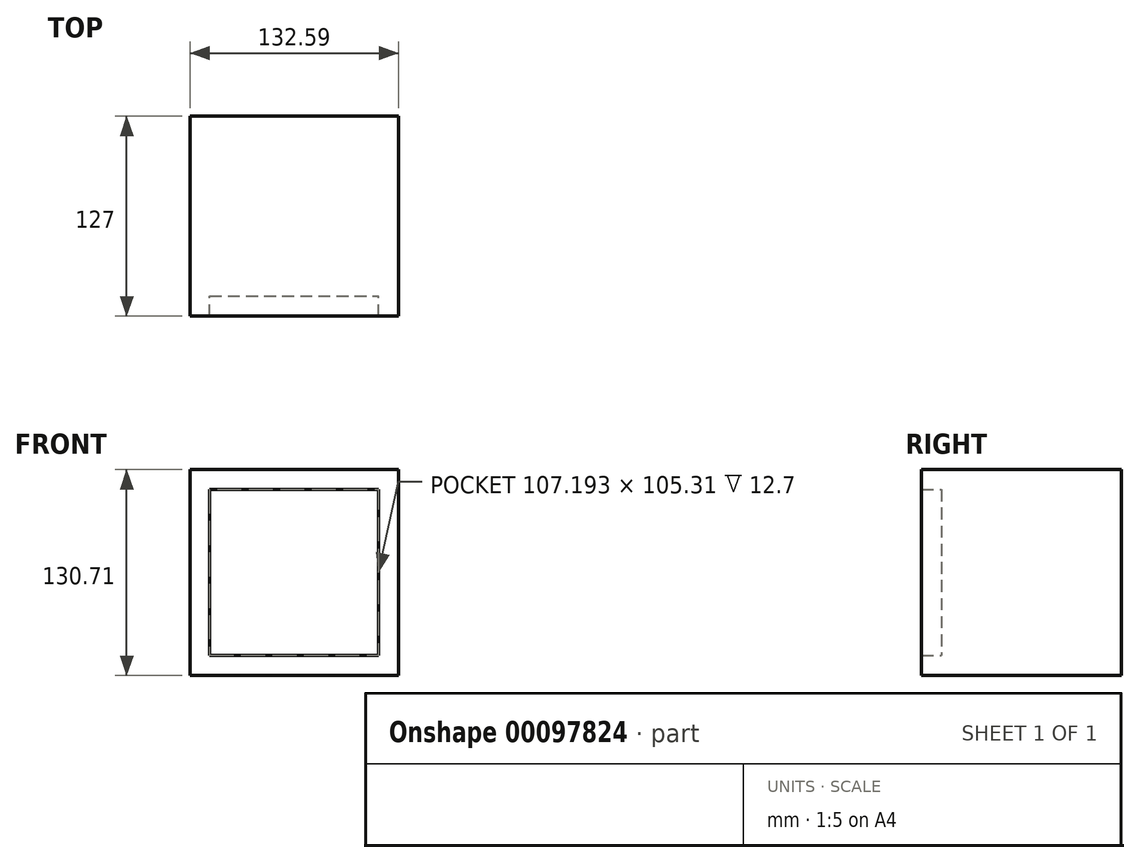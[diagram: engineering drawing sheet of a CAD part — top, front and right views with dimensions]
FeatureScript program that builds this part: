
annotation { "Feature Type Name" : "Feature", "Feature Type Description" : "" }
export const myFeature = defineFeature(function(context is Context, id is Id, definition is map)
    precondition{}
    {
        {
            var Q0;
            Q0=qCreatedBy(makeId("Front.planeOp"),FACE);
            var sketch = newSketch(context, id + "F3", { "sketchPlane" : qUnion([Q0])});
            skLineSegment(sketch, "E0.bottom", {"start": v(-65.8, 62.8) * mm, "end": v(66.78, 62.8) * mm});
            skLineSegment(sketch, "E0.top", {"start": v(-65.8, -67.92) * mm, "end": v(66.78, -67.92) * mm});
            skLineSegment(sketch, "E0.left", {"start": v(-65.8, 62.8) * mm, "end": v(-65.8, -67.92) * mm});
            skLineSegment(sketch, "E0.right", {"start": v(66.78, 62.8) * mm, "end": v(66.78, -67.92) * mm});
            skSolve(sketch);
        }
        {
            var Q0;
            Q0=makeQuery(id+"F3.imprint","IMPRINT",FACE,{"disambiguationData":[TD([[makeQuery(id+"F3.imprint","IMPRINT",EDGE,{"derivedFrom":sQuery(id+"F3.wireOp",EDGE,"E0.bottom")}),-1.0]])]});
            extrude(context, id + "F4", {"entities" : qUnion([Q0]), "depth" : 127 * mm});
        }
        {
            var Q0;
            Q0=makeQuery(id+"F4.opExtrude","CAP_FACE",FACE,{"disambiguationData":[OSD([sQuery(id+"F3.wireOp",EDGE,"E0.bottom"),sQuery(id+"F3.wireOp",EDGE,"E0.top"),sQuery(id+"F3.wireOp",EDGE,"E0.left"),sQuery(id+"F3.wireOp",EDGE,"E0.right")])],"isStart":false});
            shell(context, id + "F0", {"entities" : qUnion([Q0]), "thickness" : 12.7 * mm});
        }
        {
            var Q0;
            Q0=makeQuery(id+"F0.opShell","OFFSET_FACE",FACE,{"disambiguationData":[OSD([sQuery(id+"F3.wireOp",EDGE,"E0.bottom"),sQuery(id+"F3.wireOp",EDGE,"E0.top"),sQuery(id+"F3.wireOp",EDGE,"E0.left"),sQuery(id+"F3.wireOp",EDGE,"E0.right")])]});
            extrude(context, id + "F5", {"entities" : qUnion([Q0]), "operationType" : NewBodyOperationType.ADD, "depth" : 101.6 * mm});
        }
        {
            var Q0;
            Q0=qCreatedBy(makeId("Front.planeOp"),FACE);
            var sketch = newSketch(context, id + "F1", { "sketchPlane" : qUnion([Q0])});
            skCircle(sketch, "E1", {"center": v(0, -86.39) * mm, "radius": 5.77 * mm});
            skSolve(sketch);
        }
        {
            var Q0;
            Q0=sQuery(id+"F1.wireOp",EDGE,"E1");
            extrude(context, id + "F2", {"bodyType" : ToolBodyType.SURFACE, "surfaceEntities" : qUnion([Q0]), "depth" : 127 * mm});
        }
    });
